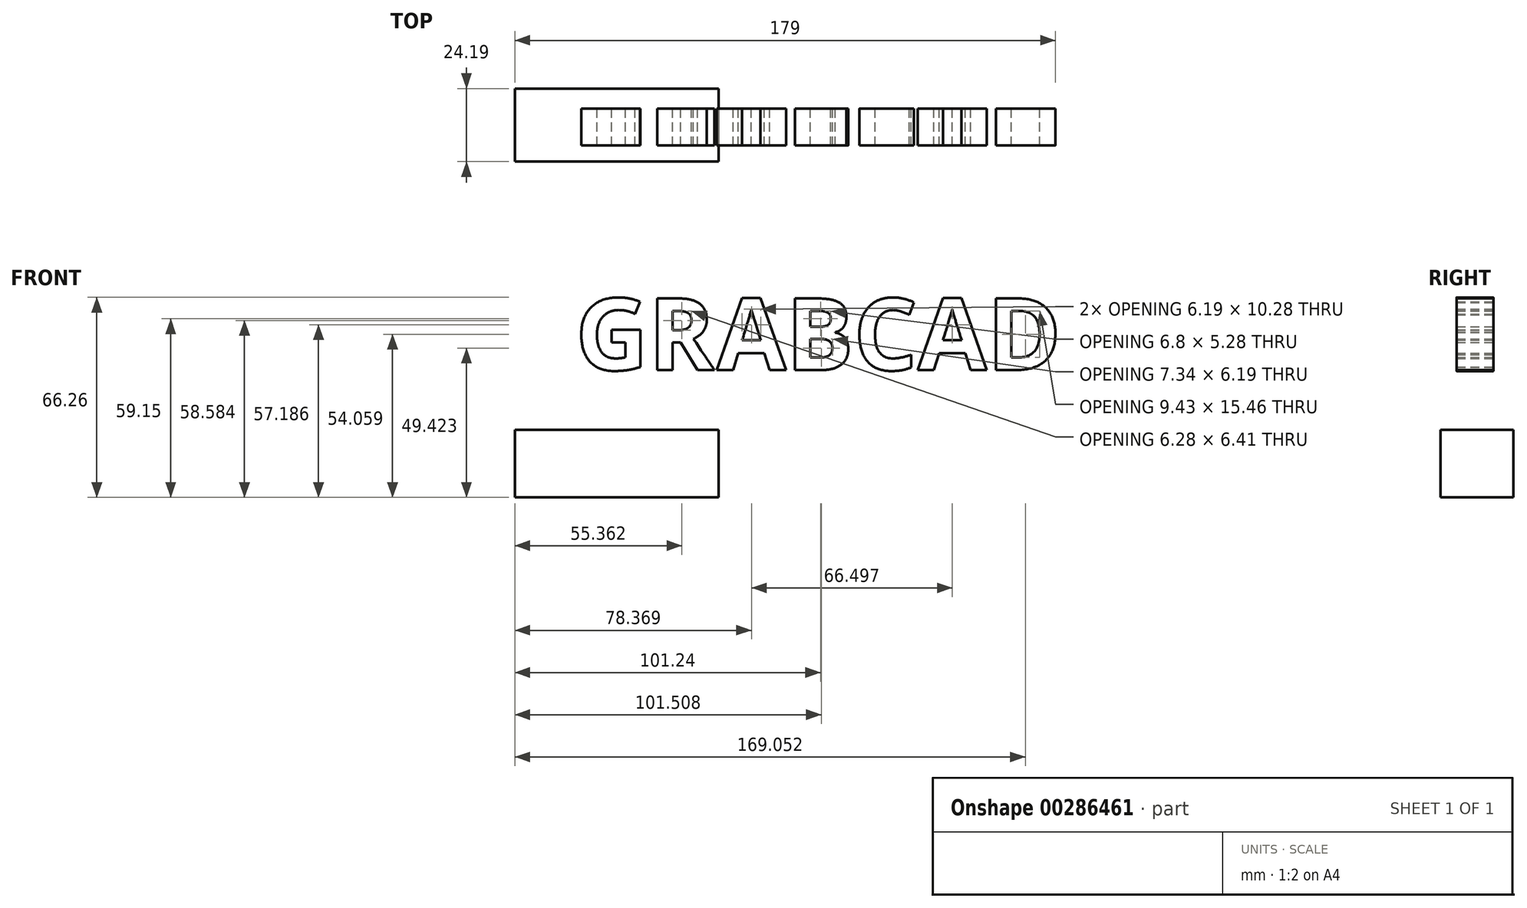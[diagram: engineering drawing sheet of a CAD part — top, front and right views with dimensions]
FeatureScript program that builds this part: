
annotation { "Feature Type Name" : "Feature", "Feature Type Description" : "" }
export const myFeature = defineFeature(function(context is Context, id is Id, definition is map)
    precondition{}
    {
        {
            var Q0;
            Q0=qCreatedBy(makeId("Front.planeOp"),FACE);
            var sketch = newSketch(context, id + "F0", { "sketchPlane" : qUnion([Q0])});
            skText(sketch, "E0", { "text": "GRABCAD", "fontName": "OpenSans-Bold.ttf"});
            const initialGuessF0  = {"E0": [-0.04739, 0, 1, 0, 0.02395]};
            skSetInitialGuess(sketch, initialGuessF0);
            skSolve(sketch);
        }
        {
            var Q0;
            Q0 = qSketchRegion(id + "F0", true);
            extrude(context, id + "F1", {"entities" : qUnion([Q0]), "depth" : 12.2 * mm});
        }
        {
            var Q0;
            Q0=qCreatedBy(makeId("Right.planeOp"),FACE);
            var sketch = newSketch(context, id + "F2", { "sketchPlane" : qUnion([Q0])});
            skLineSegment(sketch, "E1.bottom", {"start": v(6.68, -42.17) * mm, "end": v(-17.5, -42.17) * mm});
            skLineSegment(sketch, "E1.top", {"start": v(6.68, -19.77) * mm, "end": v(-17.5, -19.77) * mm});
            skLineSegment(sketch, "E1.left", {"start": v(6.68, -42.17) * mm, "end": v(6.68, -19.77) * mm});
            skLineSegment(sketch, "E1.right", {"start": v(-17.5, -42.17) * mm, "end": v(-17.5, -19.77) * mm});
            skSolve(sketch);
        }
        {
            var Q0;
            Q0 = qSketchRegion(id + "F2", true);
            extrude(context, id + "F3", {"entities" : qUnion([Q0]), "oppositeDirection" : true, "depth" : 67.5 * mm});
        }
    });
